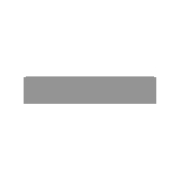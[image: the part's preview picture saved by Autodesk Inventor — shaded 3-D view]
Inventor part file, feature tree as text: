
AUTODESK INVENTOR PART (.ipt)
format: ipt  version: 2019 (Build 230136000, 136)  size: 109,056 bytes
history: native  units: mm
features: other x6, sketch x3, extrude x1
ambient origin geometry x8: Origin, YZ Plane, XZ Plane, XY Plane, X Axis, Y Axis, Z Axis, Center Point
bodies: Body1 (feature_tree)
feature tree (10):
  other  "Контрольная длина"
  other  "Генератор рам"
  other  "Твердое тело1"
  other  "Начальная плоскость"
  other  "Конечная плоскость"
  extrude  "Тело"  TaperAngle=0.0deg  [1 undecoded]
  sketch  "Эскиз"
  sketch  "Эскиз6"
  other  "РабПлоскость5"
  sketch  "Эскиз7"
note: 1 required parameter value undecoded (feature->parameter linkage not recoverable at this tier; creation-order binding heuristic only, values carry confidence <= 0.55)
